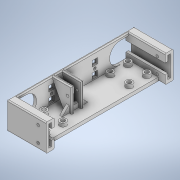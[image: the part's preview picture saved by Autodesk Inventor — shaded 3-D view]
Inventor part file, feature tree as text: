
AUTODESK INVENTOR PART (.ipt)
format: ipt  version: 2022 (Build 260153000, 153)  size: 472,064 bytes
history: native  units: in
note: dims shown in document units (in); Inventor stores cm internally (conversion verified against a paired STEP export)
features: extrude x16, sketch x16, fillet x2, mirror x1
ambient origin geometry x8: Origin, YZ Plane, XZ Plane, XY Plane, X Axis, Y Axis, Z Axis, Center Point
bodies: Solid1 (feature_tree)
feature tree (35):
  extrude  "Extrusion1"  Depth=7.4016in
  extrude  "Extrusion2"  Depth=0.1575in
  extrude  "Extrusion3"  Depth=0.1575in
  sketch  "Sketch4"  dims[d7=0.1575in d8=0.1575in]
  extrude  "Extrusion4"  Depth=0.1575in
  extrude  "Extrusion5"  Depth=0.315in
  extrude  "Extrusion6"  Depth=0.1575in
  extrude  "Extrusion7"  Depth=0.1575in
  sketch  "Sketch8"  dims[d16=0.315in d17=2.126in d18=0.0in]
  extrude  "Extrusion9"  Depth=2.126in TaperAngle=0.0deg
  extrude  "Extrusion10"  Depth=0.6102in
  extrude  "Extrusion11"  Depth=0.2362in
  extrude  "Extrusion12"  Depth=0.2362in
  extrude  "Extrusion13"  Depth=0.6299in
  extrude  "Extrusion14"  Depth=0.3937in
  extrude  "Extrusion15"  Depth=0.3937in
  mirror  "Mirror2"
  fillet  "Fillet1"  Radius=0.3937in
  extrude  "Extrusion16"  Depth=0.1969in TaperAngle=0.0deg
  extrude  "Extrusion17"  Depth=0.1575in
  fillet  "Fillet2"  Radius=0.3937in
  sketch  "Sketch1"  dims[d0=1.8898in d1=7.4016in]
  sketch  "Sketch2"  dims[d2=0.1969in d3=0.0in d4=0.1575in]
  sketch  "Sketch3"  dims[d5=0.1575in d6=0.1575in]
  sketch  "Sketch5"  dims[d9=1.378in d10=0.0in d11=0.315in]
  sketch  "Sketch6"  dims[d12=0.1575in d13=0.1575in]
  sketch  "Sketch7"  dims[d14=0.315in d15=0.1575in]
  sketch  "Sketch9"  dims[d19=0.4921in d20=0.6102in]
  sketch  "Sketch10"  dims[d21=0.2362in d22=0.2362in]
  sketch  "Sketch11"  dims[d23=0.2362in d24=0.2362in]
  sketch  "Sketch12"  dims[d25=2.126in d26=0.0in d28=0.6299in]
  sketch  "Sketch13"  dims[d29=1.378in d30=0.0in d31=0.3937in]
  sketch  "Sketch14"  dims[d32=0.3937in d33=0.3937in d34=0.3937in]
  sketch  "Sketch15"  dims[d35=0.1969in d36=0.0in d37=0.1969in d38=0.0in]
  sketch  "Sketch16"  dims[d42=0.6299in d43=0.1575in d44=0.3937in d45=0.3937in d46=1.1024in d47=0.0in d48=0.0in d49=0.1575in d50=0.7087in d51=0.0in d52=0.1575in d53=0.0in d54=0.1969in d55=0.0in d56=0.1181in d57=0.1969in d58=0.0in d59=0.1575in d60=0.1575in d61=0.4724in d62=0.0in d63=0.4528in d64=0.4528in d65=0.315in d66=0.315in d67=0.315in d68=0.315in d69=0.1575in d70=0.1575in d71=0.0in d72=0.0591in d73=2.5197in d74=3.0709in d75=0.1575in d76=1.378in d77=0.0in d78=1.378in d79=0.0in d80=0.0591in]
